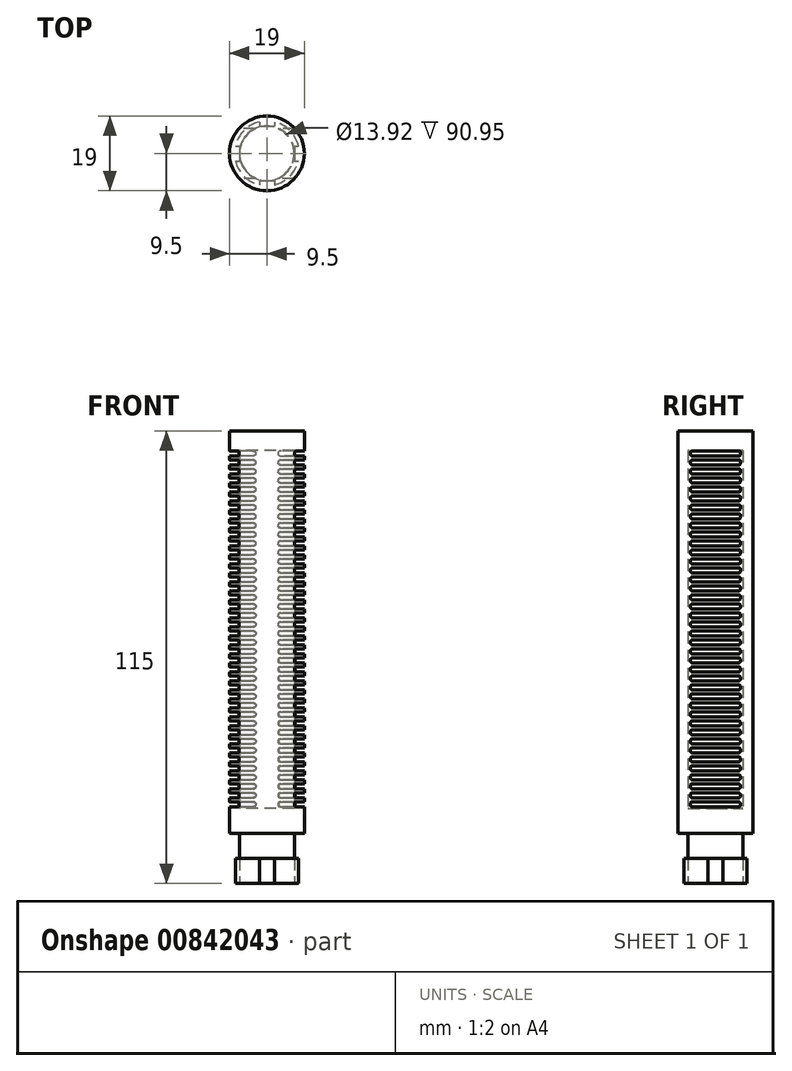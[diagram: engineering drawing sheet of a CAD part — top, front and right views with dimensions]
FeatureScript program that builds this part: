
annotation { "Feature Type Name" : "Feature", "Feature Type Description" : "" }
export const myFeature = defineFeature(function(context is Context, id is Id, definition is map)
    precondition{}
    {
        {
            var Q0;
            Q0=qCreatedBy(makeId("Top.planeOp"),FACE);
            var sketch = newSketch(context, id + "F0", { "sketchPlane" : qUnion([Q0])});
            skCircle(sketch, "E0", {"center": v(0, 0) * mm, "radius": 9.5 * mm});
            skSolve(sketch);
        }
        {
            var Q0;
            Q0=qSketchRegion(id+"F0",true);
            extrude(context, id + "F1", {"entities" : qUnion([Q0]), "depth" : 115 * mm, "offsetDistance" : 25.4 * mm});
        }
        {
            var Q0;
            Q0=qCreatedBy(makeId("Top.planeOp"),FACE);
            var sketch = newSketch(context, id + "F2", { "sketchPlane" : qUnion([Q0])});
            skCircle(sketch, "E1", {"center": v(0, 0) * mm, "radius": 9.5 * mm});
            skCircle(sketch, "E2.0", {"center": v(0, 0) * mm, "radius": 6.96 * mm});
            skSolve(sketch);
        }
        {
            var Q0;
            Q0=makeQuery(id+"F2.imprint","IMPRINT",FACE,{"disambiguationData":[TD([[makeQuery(id+"F2.imprint","IMPRINT",EDGE,{"derivedFrom":sQuery(id+"F2.wireOp",EDGE,"E1")}),1.0]])]});
            extrude(context, id + "F3", {"entities" : qUnion([Q0]), "depth" : 12.7 * mm, "offsetDistance" : 25.4 * mm, "hasSecondDirection" : true, "secondDirectionOppositeDirection" : true, "secondDirectionDepth" : -6.35 * mm});
        }
        {
            var Q0;
            Q0=makeQuery(id+"F3.opExtrude","SWEPT_BODY",BODY,{"disambiguationData":[OSD([sQuery(id+"F2.wireOp",EDGE,"E1"),sQuery(id+"F2.wireOp",EDGE,"E2.0")])]});
            var Q1;
            Q1=makeQuery(id+"F1.opExtrude","SWEPT_BODY",BODY,{"disambiguationData":[OSD([sQuery(id+"F0.wireOp",EDGE,"E0")])]});
            booleanBodies(context, id + "F4", {"operationType" : BooleanOperationType.SUBTRACTION, "tools" : qUnion([Q0]), "targets" : qUnion([Q1])});
        }
        {
            var Q0;
            Q0=qCreatedBy(makeId("Top.planeOp"),FACE);
            var sketch = newSketch(context, id + "F5", { "sketchPlane" : qUnion([Q0])});
            skCircle(sketch, "E3", {"center": v(0, 0) * mm, "radius": 9.5 * mm});
            skCircle(sketch, "E4.0", {"center": v(0, 0) * mm, "radius": 8.23 * mm});
            skSolve(sketch);
        }
        {
            var Q0;
            Q0=makeQuery(id+"F5.imprint","IMPRINT",FACE,{"disambiguationData":[TD([[makeQuery(id+"F5.imprint","IMPRINT",EDGE,{"derivedFrom":sQuery(id+"F5.wireOp",EDGE,"E3")}),1.0]])]});
            extrude(context, id + "F6", {"entities" : qUnion([Q0]), "depth" : 6.35 * mm, "offsetDistance" : 25.4 * mm});
        }
        {
            var Q0;
            Q0=makeQuery(id+"F6.opExtrude","SWEPT_BODY",BODY,{"disambiguationData":[OSD([sQuery(id+"F5.wireOp",EDGE,"E3"),sQuery(id+"F5.wireOp",EDGE,"E4.0")])]});
            var Q1;
            Q1=makeQuery(id+"F1.opExtrude","SWEPT_BODY",BODY,{"disambiguationData":[OSD([sQuery(id+"F0.wireOp",EDGE,"E0")])]});
            booleanBodies(context, id + "F7", {"operationType" : BooleanOperationType.SUBTRACTION, "tools" : qUnion([Q0]), "targets" : qUnion([Q1])});
        }
        {
            var Q0;
            Q0=qCreatedBy(makeId("Top.planeOp"),FACE);
            var sketch = newSketch(context, id + "F8", { "sketchPlane" : qUnion([Q0])});
            skCircle(sketch, "E5", {"center": v(0, 0) * mm, "radius": 9.5 * mm, "construction": true});
            skCircle(sketch, "E6.0", {"center": v(0, 0) * mm, "radius": 6.96 * mm, "construction": true});
            skLineSegment(sketch, "E7.bottom", {"start": v(-1.9, 10.77) * mm, "end": v(1.9, 10.77) * mm});
            skLineSegment(sketch, "E7.top", {"start": v(-1.9, 6.96) * mm, "end": v(1.9, 6.96) * mm});
            skLineSegment(sketch, "E7.left", {"start": v(-1.9, 10.77) * mm, "end": v(-1.9, 6.96) * mm});
            skLineSegment(sketch, "E7.right", {"start": v(1.9, 10.77) * mm, "end": v(1.9, 6.96) * mm});
            skPoint(sketch, "E8", {"position": v(0, 6.96) * mm});
            skLineSegment(sketch, "E9.bottom", {"start": v(-9.5, 9.5) * mm, "end": v(9.5, 9.5) * mm, "construction": true});
            skLineSegment(sketch, "E9.top", {"start": v(-9.5, -9.5) * mm, "end": v(9.5, -9.5) * mm, "construction": true});
            skLineSegment(sketch, "E9.left", {"start": v(-9.5, 9.5) * mm, "end": v(-9.5, -9.5) * mm, "construction": true});
            skLineSegment(sketch, "E9.right", {"start": v(9.5, 9.5) * mm, "end": v(9.5, -9.5) * mm, "construction": true});
            skPoint(sketch, "E10", {"position": v(0, -9.5) * mm});
            skPoint(sketch, "E11", {"position": v(9.5, 0) * mm});
            skLineSegment(sketch, "E12.0", {"start": v(-6.96, 6.96) * mm, "end": v(-6.96, -6.96) * mm, "construction": true});
            skLineSegment(sketch, "E12.1", {"start": v(-6.96, 6.96) * mm, "end": v(6.96, 6.96) * mm, "construction": true});
            skLineSegment(sketch, "E12.2", {"start": v(6.96, 6.96) * mm, "end": v(6.96, -6.96) * mm, "construction": true});
            skLineSegment(sketch, "E12.3", {"start": v(-6.96, -6.96) * mm, "end": v(6.96, -6.96) * mm, "construction": true});
            skLineSegment(sketch, "E13.bottom", {"start": v(6.96, 1.9) * mm, "end": v(10.77, 1.9) * mm});
            skLineSegment(sketch, "E13.top", {"start": v(6.96, -1.9) * mm, "end": v(10.77, -1.9) * mm});
            skLineSegment(sketch, "E13.left", {"start": v(6.96, 1.9) * mm, "end": v(6.96, -1.9) * mm});
            skLineSegment(sketch, "E13.right", {"start": v(10.77, 1.9) * mm, "end": v(10.77, -1.9) * mm});
            skPoint(sketch, "E14", {"position": v(6.96, 0) * mm});
            skLineSegment(sketch, "E15.bottom", {"start": v(-1.9, -6.96) * mm, "end": v(1.9, -6.96) * mm});
            skLineSegment(sketch, "E15.top", {"start": v(-1.9, -10.77) * mm, "end": v(1.9, -10.77) * mm});
            skLineSegment(sketch, "E15.left", {"start": v(-1.9, -6.96) * mm, "end": v(-1.9, -10.77) * mm});
            skLineSegment(sketch, "E15.right", {"start": v(1.9, -6.96) * mm, "end": v(1.9, -10.77) * mm});
            skPoint(sketch, "E16", {"position": v(0, -6.96) * mm});
            skLineSegment(sketch, "E17.bottom", {"start": v(-10.77, 1.9) * mm, "end": v(-6.96, 1.9) * mm});
            skLineSegment(sketch, "E17.top", {"start": v(-10.77, -1.9) * mm, "end": v(-6.96, -1.9) * mm});
            skLineSegment(sketch, "E17.left", {"start": v(-10.77, 1.9) * mm, "end": v(-10.77, -1.9) * mm});
            skLineSegment(sketch, "E17.right", {"start": v(-6.96, 1.9) * mm, "end": v(-6.96, -1.9) * mm});
            skPoint(sketch, "E18", {"position": v(-6.96, 0) * mm});
            skSolve(sketch);
        }
        {
            var Q0;
            Q0=makeQuery(id+"F8.imprint","IMPRINT",FACE,{"disambiguationData":[TD([[makeQuery(id+"F8.imprint","IMPRINT",EDGE,{"derivedFrom":sQuery(id+"F8.wireOp",EDGE,"E17.bottom")}),-1.0]])]});
            var Q1;
            Q1=makeQuery(id+"F8.imprint","IMPRINT",FACE,{"disambiguationData":[TD([[makeQuery(id+"F8.imprint","IMPRINT",EDGE,{"derivedFrom":sQuery(id+"F8.wireOp",EDGE,"E7.bottom")}),-1.0]])]});
            var Q2;
            Q2=makeQuery(id+"F8.imprint","IMPRINT",FACE,{"disambiguationData":[TD([[makeQuery(id+"F8.imprint","IMPRINT",EDGE,{"derivedFrom":sQuery(id+"F8.wireOp",EDGE,"E13.bottom")}),-1.0]])]});
            var Q3;
            Q3=makeQuery(id+"F8.imprint","IMPRINT",FACE,{"disambiguationData":[TD([[makeQuery(id+"F8.imprint","IMPRINT",EDGE,{"derivedFrom":sQuery(id+"F8.wireOp",EDGE,"E15.bottom")}),-1.0]])]});
            extrude(context, id + "F9", {"entities" : qUnion([Q0, Q1, Q2, Q3]), "depth" : 6.35 * mm, "offsetDistance" : 25.4 * mm});
        }
        {
            var Q0;
            Q0=makeQuery(id+"F9.opExtrude","SWEPT_BODY",BODY,{"disambiguationData":[OSD([sQuery(id+"F8.wireOp",EDGE,"E7.bottom"),sQuery(id+"F8.wireOp",EDGE,"E7.top"),sQuery(id+"F8.wireOp",EDGE,"E7.left"),sQuery(id+"F8.wireOp",EDGE,"E7.right")])]});
            var Q1;
            Q1=makeQuery(id+"F9.opExtrude","SWEPT_BODY",BODY,{"disambiguationData":[OSD([sQuery(id+"F8.wireOp",EDGE,"E13.bottom"),sQuery(id+"F8.wireOp",EDGE,"E13.top"),sQuery(id+"F8.wireOp",EDGE,"E13.left"),sQuery(id+"F8.wireOp",EDGE,"E13.right")])]});
            var Q2;
            Q2=makeQuery(id+"F9.opExtrude","SWEPT_BODY",BODY,{"disambiguationData":[OSD([sQuery(id+"F8.wireOp",EDGE,"E15.bottom"),sQuery(id+"F8.wireOp",EDGE,"E15.top"),sQuery(id+"F8.wireOp",EDGE,"E15.left"),sQuery(id+"F8.wireOp",EDGE,"E15.right")])]});
            var Q3;
            Q3=makeQuery(id+"F9.opExtrude","SWEPT_BODY",BODY,{"disambiguationData":[OSD([sQuery(id+"F8.wireOp",EDGE,"E17.bottom"),sQuery(id+"F8.wireOp",EDGE,"E17.top"),sQuery(id+"F8.wireOp",EDGE,"E17.left"),sQuery(id+"F8.wireOp",EDGE,"E17.right")])]});
            var Q4;
            Q4=makeQuery(id+"F1.opExtrude","SWEPT_BODY",BODY,{"disambiguationData":[OSD([sQuery(id+"F0.wireOp",EDGE,"E0")])]});
            booleanBodies(context, id + "F10", {"operationType" : BooleanOperationType.SUBTRACTION, "tools" : qUnion([Q0, Q1, Q2, Q3]), "targets" : qUnion([Q4])});
        }
        {
            var Q0;
            Q0=qCreatedBy(makeId("Top.planeOp"),FACE);
            var sketch = newSketch(context, id + "F11", { "sketchPlane" : qUnion([Q0])});
            skCircle(sketch, "E19", {"center": v(0, 0) * mm, "radius": 9.5 * mm, "construction": true});
            skCircle(sketch, "E20.0", {"center": v(0, 0) * mm, "radius": 6.96 * mm});
            skSolve(sketch);
        }
        {
            var Q0;
            Q0=makeQuery(id+"F11.imprint","IMPRINT",FACE,{"disambiguationData":[TD([[makeQuery(id+"F11.imprint","IMPRINT",EDGE,{"derivedFrom":sQuery(id+"F11.wireOp",EDGE,"E20.0")}),1.0]])]});
            extrude(context, id + "F12", {"entities" : qUnion([Q0]), "operationType" : NewBodyOperationType.REMOVE, "depth" : 110 * mm, "offsetDistance" : 25.4 * mm, "hasSecondDirection" : true, "secondDirectionOppositeDirection" : true, "secondDirectionDepth" : -19.05 * mm});
        }
        {
            var Q0;
            Q0=qCreatedBy(makeId("Right.planeOp"),FACE);
            var sketch = newSketch(context, id + "F13", { "sketchPlane" : qUnion([Q0])});
            skLineSegment(sketch, "E21.bottom", {"start": v(5.91, 109.9) * mm, "end": v(-5.91, 109.9) * mm});
            skLineSegment(sketch, "E21.top", {"start": v(5.91, 108.63) * mm, "end": v(-5.91, 108.63) * mm});
            skLineSegment(sketch, "E21.left", {"start": v(6.35, 109.46) * mm, "end": v(6.35, 109.06) * mm});
            skLineSegment(sketch, "E21.right", {"start": v(-6.35, 109.46) * mm, "end": v(-6.35, 109.06) * mm});
            skPoint(sketch, "E22", {"position": v(0, 109.9) * mm});
            skPoint(sketch, "E23.visualSharp", {"position": v(6.35, 109.9) * mm});
            skArc(sketch, "E23.filletArc", {"start": v(6.35, 109.46) * mm, "mid": v(6.22, 109.77) * mm, "end": v(5.91, 109.9) * mm});
            skPoint(sketch, "E24.visualSharp", {"position": v(6.35, 108.63) * mm});
            skArc(sketch, "E24.filletArc", {"start": v(5.91, 108.63) * mm, "mid": v(6.22, 108.75) * mm, "end": v(6.35, 109.06) * mm});
            skPoint(sketch, "E25.visualSharp", {"position": v(-6.35, 108.63) * mm});
            skArc(sketch, "E25.filletArc", {"start": v(-6.35, 109.06) * mm, "mid": v(-6.22, 108.75) * mm, "end": v(-5.91, 108.63) * mm});
            skPoint(sketch, "E26.visualSharp", {"position": v(-6.35, 109.9) * mm});
            skArc(sketch, "E26.filletArc", {"start": v(-5.91, 109.9) * mm, "mid": v(-6.22, 109.77) * mm, "end": v(-6.35, 109.46) * mm});
            skArc(sketch, "E27.1.0.0", {"start": v(6.35, 107.17) * mm, "mid": v(6.22, 107.48) * mm, "end": v(5.9, 107.6) * mm});
            skLineSegment(sketch, "E27.1.0.1", {"start": v(5.9, 107.6) * mm, "end": v(-5.91, 107.6) * mm});
            skArc(sketch, "E27.1.0.2", {"start": v(-5.91, 107.6) * mm, "mid": v(-6.22, 107.48) * mm, "end": v(-6.35, 107.17) * mm});
            skLineSegment(sketch, "E27.1.0.3", {"start": v(-6.35, 107.17) * mm, "end": v(-6.35, 106.78) * mm});
            skArc(sketch, "E27.1.0.4", {"start": v(-6.35, 106.78) * mm, "mid": v(-6.22, 106.47) * mm, "end": v(-5.91, 106.34) * mm});
            skLineSegment(sketch, "E27.1.0.5", {"start": v(5.9, 106.34) * mm, "end": v(-5.91, 106.34) * mm});
            skArc(sketch, "E27.1.0.6", {"start": v(5.9, 106.34) * mm, "mid": v(6.22, 106.47) * mm, "end": v(6.35, 106.78) * mm});
            skLineSegment(sketch, "E27.1.0.7", {"start": v(6.35, 107.17) * mm, "end": v(6.35, 106.78) * mm});
            skArc(sketch, "E27.2.0.0", {"start": v(6.35, 104.88) * mm, "mid": v(6.22, 105.2) * mm, "end": v(5.9, 105.32) * mm});
            skLineSegment(sketch, "E27.2.0.1", {"start": v(5.9, 105.32) * mm, "end": v(-5.91, 105.32) * mm});
            skArc(sketch, "E27.2.0.2", {"start": v(-5.91, 105.32) * mm, "mid": v(-6.22, 105.2) * mm, "end": v(-6.35, 104.88) * mm});
            skLineSegment(sketch, "E27.2.0.3", {"start": v(-6.35, 104.88) * mm, "end": v(-6.35, 104.5) * mm});
            skArc(sketch, "E27.2.0.4", {"start": v(-6.35, 104.5) * mm, "mid": v(-6.22, 104.18) * mm, "end": v(-5.91, 104.05) * mm});
            skLineSegment(sketch, "E27.2.0.5", {"start": v(5.9, 104.05) * mm, "end": v(-5.91, 104.05) * mm});
            skArc(sketch, "E27.2.0.6", {"start": v(5.9, 104.05) * mm, "mid": v(6.22, 104.18) * mm, "end": v(6.35, 104.5) * mm});
            skLineSegment(sketch, "E27.2.0.7", {"start": v(6.35, 104.88) * mm, "end": v(6.35, 104.5) * mm});
            skArc(sketch, "E27.3.0.0", {"start": v(6.35, 102.6) * mm, "mid": v(6.22, 102.9) * mm, "end": v(5.9, 103.04) * mm});
            skLineSegment(sketch, "E27.3.0.1", {"start": v(5.9, 103.04) * mm, "end": v(-5.91, 103.04) * mm});
            skArc(sketch, "E27.3.0.2", {"start": v(-5.91, 103.04) * mm, "mid": v(-6.22, 102.9) * mm, "end": v(-6.35, 102.6) * mm});
            skLineSegment(sketch, "E27.3.0.3", {"start": v(-6.35, 102.6) * mm, "end": v(-6.35, 102.2) * mm});
            skArc(sketch, "E27.3.0.4", {"start": v(-6.35, 102.2) * mm, "mid": v(-6.22, 101.9) * mm, "end": v(-5.91, 101.77) * mm});
            skLineSegment(sketch, "E27.3.0.5", {"start": v(5.9, 101.77) * mm, "end": v(-5.91, 101.77) * mm});
            skArc(sketch, "E27.3.0.6", {"start": v(5.9, 101.77) * mm, "mid": v(6.22, 101.9) * mm, "end": v(6.35, 102.2) * mm});
            skLineSegment(sketch, "E27.3.0.7", {"start": v(6.35, 102.6) * mm, "end": v(6.35, 102.2) * mm});
            skArc(sketch, "E27.4.0.0", {"start": v(6.35, 100.31) * mm, "mid": v(6.22, 100.62) * mm, "end": v(5.9, 100.75) * mm});
            skLineSegment(sketch, "E27.4.0.1", {"start": v(5.9, 100.75) * mm, "end": v(-5.91, 100.75) * mm});
            skArc(sketch, "E27.4.0.2", {"start": v(-5.91, 100.75) * mm, "mid": v(-6.22, 100.62) * mm, "end": v(-6.35, 100.31) * mm});
            skLineSegment(sketch, "E27.4.0.3", {"start": v(-6.35, 100.31) * mm, "end": v(-6.35, 99.92) * mm});
            skArc(sketch, "E27.4.0.4", {"start": v(-6.35, 99.92) * mm, "mid": v(-6.22, 99.61) * mm, "end": v(-5.91, 99.48) * mm});
            skLineSegment(sketch, "E27.4.0.5", {"start": v(5.9, 99.48) * mm, "end": v(-5.91, 99.48) * mm});
            skArc(sketch, "E27.4.0.6", {"start": v(5.9, 99.48) * mm, "mid": v(6.22, 99.61) * mm, "end": v(6.35, 99.92) * mm});
            skLineSegment(sketch, "E27.4.0.7", {"start": v(6.35, 100.31) * mm, "end": v(6.35, 99.92) * mm});
            skArc(sketch, "E27.5.0.0", {"start": v(6.35, 98.03) * mm, "mid": v(6.22, 98.34) * mm, "end": v(5.9, 98.47) * mm});
            skLineSegment(sketch, "E27.5.0.1", {"start": v(5.9, 98.47) * mm, "end": v(-5.91, 98.47) * mm});
            skArc(sketch, "E27.5.0.2", {"start": v(-5.91, 98.47) * mm, "mid": v(-6.23, 98.34) * mm, "end": v(-6.35, 98.03) * mm});
            skLineSegment(sketch, "E27.5.0.3", {"start": v(-6.35, 98.03) * mm, "end": v(-6.35, 97.63) * mm});
            skArc(sketch, "E27.5.0.4", {"start": v(-6.35, 97.63) * mm, "mid": v(-6.23, 97.32) * mm, "end": v(-5.91, 97.2) * mm});
            skLineSegment(sketch, "E27.5.0.5", {"start": v(5.9, 97.2) * mm, "end": v(-5.91, 97.2) * mm});
            skArc(sketch, "E27.5.0.6", {"start": v(5.9, 97.2) * mm, "mid": v(6.22, 97.32) * mm, "end": v(6.35, 97.63) * mm});
            skLineSegment(sketch, "E27.5.0.7", {"start": v(6.35, 98.03) * mm, "end": v(6.35, 97.63) * mm});
            skArc(sketch, "E27.6.0.0", {"start": v(6.34, 95.74) * mm, "mid": v(6.22, 96.05) * mm, "end": v(5.9, 96.18) * mm});
            skLineSegment(sketch, "E27.6.0.1", {"start": v(5.9, 96.18) * mm, "end": v(-5.92, 96.18) * mm});
            skArc(sketch, "E27.6.0.2", {"start": v(-5.92, 96.18) * mm, "mid": v(-6.23, 96.05) * mm, "end": v(-6.36, 95.74) * mm});
            skLineSegment(sketch, "E27.6.0.3", {"start": v(-6.36, 95.74) * mm, "end": v(-6.36, 95.35) * mm});
            skArc(sketch, "E27.6.0.4", {"start": v(-6.36, 95.35) * mm, "mid": v(-6.23, 95.04) * mm, "end": v(-5.92, 94.9) * mm});
            skLineSegment(sketch, "E27.6.0.5", {"start": v(5.9, 94.9) * mm, "end": v(-5.92, 94.9) * mm});
            skArc(sketch, "E27.6.0.6", {"start": v(5.9, 94.9) * mm, "mid": v(6.22, 95.04) * mm, "end": v(6.34, 95.35) * mm});
            skLineSegment(sketch, "E27.6.0.7", {"start": v(6.34, 95.74) * mm, "end": v(6.34, 95.35) * mm});
            skArc(sketch, "E27.7.0.0", {"start": v(6.34, 93.45) * mm, "mid": v(6.22, 93.77) * mm, "end": v(5.9, 93.9) * mm});
            skLineSegment(sketch, "E27.7.0.1", {"start": v(5.9, 93.9) * mm, "end": v(-5.92, 93.9) * mm});
            skArc(sketch, "E27.7.0.2", {"start": v(-5.92, 93.9) * mm, "mid": v(-6.23, 93.77) * mm, "end": v(-6.36, 93.45) * mm});
            skLineSegment(sketch, "E27.7.0.3", {"start": v(-6.36, 93.45) * mm, "end": v(-6.36, 93.06) * mm});
            skArc(sketch, "E27.7.0.4", {"start": v(-6.36, 93.06) * mm, "mid": v(-6.23, 92.75) * mm, "end": v(-5.92, 92.62) * mm});
            skLineSegment(sketch, "E27.7.0.5", {"start": v(5.9, 92.62) * mm, "end": v(-5.92, 92.62) * mm});
            skArc(sketch, "E27.7.0.6", {"start": v(5.9, 92.62) * mm, "mid": v(6.22, 92.75) * mm, "end": v(6.34, 93.06) * mm});
            skLineSegment(sketch, "E27.7.0.7", {"start": v(6.34, 93.45) * mm, "end": v(6.34, 93.06) * mm});
            skArc(sketch, "E27.8.0.0", {"start": v(6.34, 91.17) * mm, "mid": v(6.21, 91.48) * mm, "end": v(5.9, 91.6) * mm});
            skLineSegment(sketch, "E27.8.0.1", {"start": v(5.9, 91.6) * mm, "end": v(-5.92, 91.6) * mm});
            skArc(sketch, "E27.8.0.2", {"start": v(-5.92, 91.6) * mm, "mid": v(-6.23, 91.48) * mm, "end": v(-6.36, 91.17) * mm});
            skLineSegment(sketch, "E27.8.0.3", {"start": v(-6.36, 91.17) * mm, "end": v(-6.36, 90.78) * mm});
            skArc(sketch, "E27.8.0.4", {"start": v(-6.36, 90.78) * mm, "mid": v(-6.23, 90.47) * mm, "end": v(-5.92, 90.34) * mm});
            skLineSegment(sketch, "E27.8.0.5", {"start": v(5.9, 90.34) * mm, "end": v(-5.92, 90.34) * mm});
            skArc(sketch, "E27.8.0.6", {"start": v(5.9, 90.34) * mm, "mid": v(6.21, 90.47) * mm, "end": v(6.34, 90.78) * mm});
            skLineSegment(sketch, "E27.8.0.7", {"start": v(6.34, 91.17) * mm, "end": v(6.34, 90.78) * mm});
            skArc(sketch, "E27.9.0.0", {"start": v(6.34, 88.88) * mm, "mid": v(6.21, 89.2) * mm, "end": v(5.9, 89.32) * mm});
            skLineSegment(sketch, "E27.9.0.1", {"start": v(5.9, 89.32) * mm, "end": v(-5.92, 89.32) * mm});
            skArc(sketch, "E27.9.0.2", {"start": v(-5.92, 89.32) * mm, "mid": v(-6.23, 89.2) * mm, "end": v(-6.36, 88.88) * mm});
            skLineSegment(sketch, "E27.9.0.3", {"start": v(-6.36, 88.88) * mm, "end": v(-6.36, 88.5) * mm});
            skArc(sketch, "E27.9.0.4", {"start": v(-6.36, 88.5) * mm, "mid": v(-6.23, 88.18) * mm, "end": v(-5.92, 88.05) * mm});
            skLineSegment(sketch, "E27.9.0.5", {"start": v(5.9, 88.05) * mm, "end": v(-5.92, 88.05) * mm});
            skArc(sketch, "E27.9.0.6", {"start": v(5.9, 88.05) * mm, "mid": v(6.21, 88.18) * mm, "end": v(6.34, 88.5) * mm});
            skLineSegment(sketch, "E27.9.0.7", {"start": v(6.34, 88.88) * mm, "end": v(6.34, 88.5) * mm});
            skArc(sketch, "E27.10.0.0", {"start": v(6.34, 86.6) * mm, "mid": v(6.21, 86.9) * mm, "end": v(5.9, 87.04) * mm});
            skLineSegment(sketch, "E27.10.0.1", {"start": v(5.9, 87.04) * mm, "end": v(-5.92, 87.04) * mm});
            skArc(sketch, "E27.10.0.2", {"start": v(-5.92, 87.04) * mm, "mid": v(-6.23, 86.9) * mm, "end": v(-6.36, 86.6) * mm});
            skLineSegment(sketch, "E27.10.0.3", {"start": v(-6.36, 86.6) * mm, "end": v(-6.36, 86.2) * mm});
            skArc(sketch, "E27.10.0.4", {"start": v(-6.36, 86.2) * mm, "mid": v(-6.23, 85.9) * mm, "end": v(-5.92, 85.77) * mm});
            skLineSegment(sketch, "E27.10.0.5", {"start": v(5.9, 85.77) * mm, "end": v(-5.92, 85.77) * mm});
            skArc(sketch, "E27.10.0.6", {"start": v(5.9, 85.77) * mm, "mid": v(6.21, 85.9) * mm, "end": v(6.34, 86.2) * mm});
            skLineSegment(sketch, "E27.10.0.7", {"start": v(6.34, 86.6) * mm, "end": v(6.34, 86.2) * mm});
            skArc(sketch, "E27.11.0.0", {"start": v(6.34, 84.31) * mm, "mid": v(6.21, 84.62) * mm, "end": v(5.9, 84.75) * mm});
            skLineSegment(sketch, "E27.11.0.1", {"start": v(5.9, 84.75) * mm, "end": v(-5.92, 84.75) * mm});
            skArc(sketch, "E27.11.0.2", {"start": v(-5.92, 84.75) * mm, "mid": v(-6.23, 84.62) * mm, "end": v(-6.36, 84.31) * mm});
            skLineSegment(sketch, "E27.11.0.3", {"start": v(-6.36, 84.31) * mm, "end": v(-6.36, 83.92) * mm});
            skArc(sketch, "E27.11.0.4", {"start": v(-6.36, 83.92) * mm, "mid": v(-6.23, 83.6) * mm, "end": v(-5.92, 83.48) * mm});
            skLineSegment(sketch, "E27.11.0.5", {"start": v(5.9, 83.48) * mm, "end": v(-5.92, 83.48) * mm});
            skArc(sketch, "E27.11.0.6", {"start": v(5.9, 83.48) * mm, "mid": v(6.21, 83.6) * mm, "end": v(6.34, 83.92) * mm});
            skLineSegment(sketch, "E27.11.0.7", {"start": v(6.34, 84.31) * mm, "end": v(6.34, 83.92) * mm});
            skArc(sketch, "E27.12.0.0", {"start": v(6.34, 82.02) * mm, "mid": v(6.21, 82.34) * mm, "end": v(5.9, 82.46) * mm});
            skLineSegment(sketch, "E27.12.0.1", {"start": v(5.9, 82.46) * mm, "end": v(-5.92, 82.46) * mm});
            skArc(sketch, "E27.12.0.2", {"start": v(-5.92, 82.46) * mm, "mid": v(-6.23, 82.34) * mm, "end": v(-6.36, 82.02) * mm});
            skLineSegment(sketch, "E27.12.0.3", {"start": v(-6.36, 82.02) * mm, "end": v(-6.36, 81.63) * mm});
            skArc(sketch, "E27.12.0.4", {"start": v(-6.36, 81.63) * mm, "mid": v(-6.23, 81.32) * mm, "end": v(-5.92, 81.2) * mm});
            skLineSegment(sketch, "E27.12.0.5", {"start": v(5.9, 81.2) * mm, "end": v(-5.92, 81.2) * mm});
            skArc(sketch, "E27.12.0.6", {"start": v(5.9, 81.2) * mm, "mid": v(6.21, 81.32) * mm, "end": v(6.34, 81.63) * mm});
            skLineSegment(sketch, "E27.12.0.7", {"start": v(6.34, 82.02) * mm, "end": v(6.34, 81.63) * mm});
            skArc(sketch, "E27.13.0.0", {"start": v(6.34, 79.74) * mm, "mid": v(6.21, 80.05) * mm, "end": v(5.9, 80.18) * mm});
            skLineSegment(sketch, "E27.13.0.1", {"start": v(5.9, 80.18) * mm, "end": v(-5.92, 80.18) * mm});
            skArc(sketch, "E27.13.0.2", {"start": v(-5.92, 80.18) * mm, "mid": v(-6.23, 80.05) * mm, "end": v(-6.36, 79.74) * mm});
            skLineSegment(sketch, "E27.13.0.3", {"start": v(-6.36, 79.74) * mm, "end": v(-6.36, 79.35) * mm});
            skArc(sketch, "E27.13.0.4", {"start": v(-6.36, 79.35) * mm, "mid": v(-6.23, 79.04) * mm, "end": v(-5.92, 78.9) * mm});
            skLineSegment(sketch, "E27.13.0.5", {"start": v(5.9, 78.9) * mm, "end": v(-5.92, 78.9) * mm});
            skArc(sketch, "E27.13.0.6", {"start": v(5.9, 78.9) * mm, "mid": v(6.21, 79.04) * mm, "end": v(6.34, 79.35) * mm});
            skLineSegment(sketch, "E27.13.0.7", {"start": v(6.34, 79.74) * mm, "end": v(6.34, 79.35) * mm});
            skArc(sketch, "E27.14.0.0", {"start": v(6.34, 77.45) * mm, "mid": v(6.2, 77.76) * mm, "end": v(5.9, 77.9) * mm});
            skLineSegment(sketch, "E27.14.0.1", {"start": v(5.9, 77.9) * mm, "end": v(-5.92, 77.9) * mm});
            skArc(sketch, "E27.14.0.2", {"start": v(-5.92, 77.9) * mm, "mid": v(-6.23, 77.76) * mm, "end": v(-6.36, 77.45) * mm});
            skLineSegment(sketch, "E27.14.0.3", {"start": v(-6.36, 77.45) * mm, "end": v(-6.36, 77.06) * mm});
            skArc(sketch, "E27.14.0.4", {"start": v(-6.36, 77.06) * mm, "mid": v(-6.23, 76.75) * mm, "end": v(-5.92, 76.62) * mm});
            skLineSegment(sketch, "E27.14.0.5", {"start": v(5.9, 76.62) * mm, "end": v(-5.92, 76.62) * mm});
            skArc(sketch, "E27.14.0.6", {"start": v(5.9, 76.62) * mm, "mid": v(6.2, 76.75) * mm, "end": v(6.34, 77.06) * mm});
            skLineSegment(sketch, "E27.14.0.7", {"start": v(6.34, 77.45) * mm, "end": v(6.34, 77.06) * mm});
            skArc(sketch, "E27.15.0.0", {"start": v(6.34, 75.17) * mm, "mid": v(6.2, 75.48) * mm, "end": v(5.9, 75.6) * mm});
            skLineSegment(sketch, "E27.15.0.1", {"start": v(5.9, 75.6) * mm, "end": v(-5.92, 75.6) * mm});
            skArc(sketch, "E27.15.0.2", {"start": v(-5.92, 75.6) * mm, "mid": v(-6.23, 75.48) * mm, "end": v(-6.36, 75.17) * mm});
            skLineSegment(sketch, "E27.15.0.3", {"start": v(-6.36, 75.17) * mm, "end": v(-6.36, 74.77) * mm});
            skArc(sketch, "E27.15.0.4", {"start": v(-6.36, 74.77) * mm, "mid": v(-6.23, 74.46) * mm, "end": v(-5.92, 74.34) * mm});
            skLineSegment(sketch, "E27.15.0.5", {"start": v(5.9, 74.34) * mm, "end": v(-5.92, 74.34) * mm});
            skArc(sketch, "E27.15.0.6", {"start": v(5.9, 74.34) * mm, "mid": v(6.2, 74.46) * mm, "end": v(6.34, 74.77) * mm});
            skLineSegment(sketch, "E27.15.0.7", {"start": v(6.34, 75.17) * mm, "end": v(6.34, 74.77) * mm});
            skArc(sketch, "E27.16.0.0", {"start": v(6.34, 72.88) * mm, "mid": v(6.2, 73.2) * mm, "end": v(5.9, 73.32) * mm});
            skLineSegment(sketch, "E27.16.0.1", {"start": v(5.9, 73.32) * mm, "end": v(-5.92, 73.32) * mm});
            skArc(sketch, "E27.16.0.2", {"start": v(-5.92, 73.32) * mm, "mid": v(-6.23, 73.2) * mm, "end": v(-6.36, 72.88) * mm});
            skLineSegment(sketch, "E27.16.0.3", {"start": v(-6.36, 72.88) * mm, "end": v(-6.36, 72.49) * mm});
            skArc(sketch, "E27.16.0.4", {"start": v(-6.36, 72.49) * mm, "mid": v(-6.23, 72.18) * mm, "end": v(-5.92, 72.05) * mm});
            skLineSegment(sketch, "E27.16.0.5", {"start": v(5.9, 72.05) * mm, "end": v(-5.92, 72.05) * mm});
            skArc(sketch, "E27.16.0.6", {"start": v(5.9, 72.05) * mm, "mid": v(6.2, 72.18) * mm, "end": v(6.34, 72.49) * mm});
            skLineSegment(sketch, "E27.16.0.7", {"start": v(6.34, 72.88) * mm, "end": v(6.34, 72.49) * mm});
            skArc(sketch, "E27.17.0.0", {"start": v(6.34, 70.6) * mm, "mid": v(6.2, 70.9) * mm, "end": v(5.9, 71.03) * mm});
            skLineSegment(sketch, "E27.17.0.1", {"start": v(5.9, 71.03) * mm, "end": v(-5.93, 71.03) * mm});
            skArc(sketch, "E27.17.0.2", {"start": v(-5.93, 71.03) * mm, "mid": v(-6.24, 70.9) * mm, "end": v(-6.36, 70.6) * mm});
            skLineSegment(sketch, "E27.17.0.3", {"start": v(-6.36, 70.6) * mm, "end": v(-6.36, 70.2) * mm});
            skArc(sketch, "E27.17.0.4", {"start": v(-6.36, 70.2) * mm, "mid": v(-6.24, 69.9) * mm, "end": v(-5.93, 69.76) * mm});
            skLineSegment(sketch, "E27.17.0.5", {"start": v(5.9, 69.76) * mm, "end": v(-5.93, 69.76) * mm});
            skArc(sketch, "E27.17.0.6", {"start": v(5.9, 69.76) * mm, "mid": v(6.2, 69.9) * mm, "end": v(6.34, 70.2) * mm});
            skLineSegment(sketch, "E27.17.0.7", {"start": v(6.34, 70.6) * mm, "end": v(6.34, 70.2) * mm});
            skArc(sketch, "E27.18.0.0", {"start": v(6.33, 68.3) * mm, "mid": v(6.2, 68.62) * mm, "end": v(5.9, 68.75) * mm});
            skLineSegment(sketch, "E27.18.0.1", {"start": v(5.9, 68.75) * mm, "end": v(-5.93, 68.75) * mm});
            skArc(sketch, "E27.18.0.2", {"start": v(-5.93, 68.75) * mm, "mid": v(-6.24, 68.62) * mm, "end": v(-6.37, 68.3) * mm});
            skLineSegment(sketch, "E27.18.0.3", {"start": v(-6.37, 68.3) * mm, "end": v(-6.37, 67.92) * mm});
            skArc(sketch, "E27.18.0.4", {"start": v(-6.37, 67.92) * mm, "mid": v(-6.24, 67.6) * mm, "end": v(-5.93, 67.48) * mm});
            skLineSegment(sketch, "E27.18.0.5", {"start": v(5.9, 67.48) * mm, "end": v(-5.93, 67.48) * mm});
            skArc(sketch, "E27.18.0.6", {"start": v(5.9, 67.48) * mm, "mid": v(6.2, 67.6) * mm, "end": v(6.33, 67.92) * mm});
            skLineSegment(sketch, "E27.18.0.7", {"start": v(6.33, 68.3) * mm, "end": v(6.33, 67.92) * mm});
            skArc(sketch, "E27.19.0.0", {"start": v(6.33, 66.02) * mm, "mid": v(6.2, 66.33) * mm, "end": v(5.9, 66.46) * mm});
            skLineSegment(sketch, "E27.19.0.1", {"start": v(5.9, 66.46) * mm, "end": v(-5.93, 66.46) * mm});
            skArc(sketch, "E27.19.0.2", {"start": v(-5.93, 66.46) * mm, "mid": v(-6.24, 66.33) * mm, "end": v(-6.37, 66.02) * mm});
            skLineSegment(sketch, "E27.19.0.3", {"start": v(-6.37, 66.02) * mm, "end": v(-6.37, 65.63) * mm});
            skArc(sketch, "E27.19.0.4", {"start": v(-6.37, 65.63) * mm, "mid": v(-6.24, 65.32) * mm, "end": v(-5.93, 65.2) * mm});
            skLineSegment(sketch, "E27.19.0.5", {"start": v(5.9, 65.2) * mm, "end": v(-5.93, 65.2) * mm});
            skArc(sketch, "E27.19.0.6", {"start": v(5.9, 65.2) * mm, "mid": v(6.2, 65.32) * mm, "end": v(6.33, 65.63) * mm});
            skLineSegment(sketch, "E27.19.0.7", {"start": v(6.33, 66.02) * mm, "end": v(6.33, 65.63) * mm});
            skArc(sketch, "E27.20.0.0", {"start": v(6.33, 63.74) * mm, "mid": v(6.2, 64.05) * mm, "end": v(5.9, 64.18) * mm});
            skLineSegment(sketch, "E27.20.0.1", {"start": v(5.9, 64.18) * mm, "end": v(-5.93, 64.18) * mm});
            skArc(sketch, "E27.20.0.2", {"start": v(-5.93, 64.18) * mm, "mid": v(-6.24, 64.05) * mm, "end": v(-6.37, 63.74) * mm});
            skLineSegment(sketch, "E27.20.0.3", {"start": v(-6.37, 63.74) * mm, "end": v(-6.37, 63.34) * mm});
            skArc(sketch, "E27.20.0.4", {"start": v(-6.37, 63.34) * mm, "mid": v(-6.24, 63.03) * mm, "end": v(-5.93, 62.9) * mm});
            skLineSegment(sketch, "E27.20.0.5", {"start": v(5.9, 62.9) * mm, "end": v(-5.93, 62.9) * mm});
            skArc(sketch, "E27.20.0.6", {"start": v(5.9, 62.9) * mm, "mid": v(6.2, 63.03) * mm, "end": v(6.33, 63.34) * mm});
            skLineSegment(sketch, "E27.20.0.7", {"start": v(6.33, 63.74) * mm, "end": v(6.33, 63.34) * mm});
            skArc(sketch, "E27.21.0.0", {"start": v(6.33, 61.45) * mm, "mid": v(6.2, 61.76) * mm, "end": v(5.9, 61.89) * mm});
            skLineSegment(sketch, "E27.21.0.1", {"start": v(5.9, 61.89) * mm, "end": v(-5.93, 61.89) * mm});
            skArc(sketch, "E27.21.0.2", {"start": v(-5.93, 61.89) * mm, "mid": v(-6.24, 61.76) * mm, "end": v(-6.37, 61.45) * mm});
            skLineSegment(sketch, "E27.21.0.3", {"start": v(-6.37, 61.45) * mm, "end": v(-6.37, 61.06) * mm});
            skArc(sketch, "E27.21.0.4", {"start": v(-6.37, 61.06) * mm, "mid": v(-6.24, 60.75) * mm, "end": v(-5.93, 60.62) * mm});
            skLineSegment(sketch, "E27.21.0.5", {"start": v(5.9, 60.62) * mm, "end": v(-5.93, 60.62) * mm});
            skArc(sketch, "E27.21.0.6", {"start": v(5.9, 60.62) * mm, "mid": v(6.2, 60.75) * mm, "end": v(6.33, 61.06) * mm});
            skLineSegment(sketch, "E27.21.0.7", {"start": v(6.33, 61.45) * mm, "end": v(6.33, 61.06) * mm});
            skArc(sketch, "E27.22.0.0", {"start": v(6.33, 59.16) * mm, "mid": v(6.2, 59.48) * mm, "end": v(5.9, 59.6) * mm});
            skLineSegment(sketch, "E27.22.0.1", {"start": v(5.9, 59.6) * mm, "end": v(-5.93, 59.6) * mm});
            skArc(sketch, "E27.22.0.2", {"start": v(-5.93, 59.6) * mm, "mid": v(-6.24, 59.48) * mm, "end": v(-6.37, 59.16) * mm});
            skLineSegment(sketch, "E27.22.0.3", {"start": v(-6.37, 59.16) * mm, "end": v(-6.37, 58.77) * mm});
            skArc(sketch, "E27.22.0.4", {"start": v(-6.37, 58.77) * mm, "mid": v(-6.24, 58.46) * mm, "end": v(-5.93, 58.33) * mm});
            skLineSegment(sketch, "E27.22.0.5", {"start": v(5.9, 58.33) * mm, "end": v(-5.93, 58.33) * mm});
            skArc(sketch, "E27.22.0.6", {"start": v(5.9, 58.33) * mm, "mid": v(6.2, 58.46) * mm, "end": v(6.33, 58.77) * mm});
            skLineSegment(sketch, "E27.22.0.7", {"start": v(6.33, 59.16) * mm, "end": v(6.33, 58.77) * mm});
            skArc(sketch, "E27.23.0.0", {"start": v(6.33, 56.88) * mm, "mid": v(6.2, 57.19) * mm, "end": v(5.9, 57.32) * mm});
            skLineSegment(sketch, "E27.23.0.1", {"start": v(5.9, 57.32) * mm, "end": v(-5.93, 57.32) * mm});
            skArc(sketch, "E27.23.0.2", {"start": v(-5.93, 57.32) * mm, "mid": v(-6.24, 57.19) * mm, "end": v(-6.37, 56.88) * mm});
            skLineSegment(sketch, "E27.23.0.3", {"start": v(-6.37, 56.88) * mm, "end": v(-6.37, 56.49) * mm});
            skArc(sketch, "E27.23.0.4", {"start": v(-6.37, 56.49) * mm, "mid": v(-6.24, 56.18) * mm, "end": v(-5.93, 56.05) * mm});
            skLineSegment(sketch, "E27.23.0.5", {"start": v(5.9, 56.05) * mm, "end": v(-5.93, 56.05) * mm});
            skArc(sketch, "E27.23.0.6", {"start": v(5.9, 56.05) * mm, "mid": v(6.2, 56.18) * mm, "end": v(6.33, 56.49) * mm});
            skLineSegment(sketch, "E27.23.0.7", {"start": v(6.33, 56.88) * mm, "end": v(6.33, 56.49) * mm});
            skArc(sketch, "E27.24.0.0", {"start": v(6.33, 54.6) * mm, "mid": v(6.2, 54.9) * mm, "end": v(5.9, 55.03) * mm});
            skLineSegment(sketch, "E27.24.0.1", {"start": v(5.9, 55.03) * mm, "end": v(-5.93, 55.03) * mm});
            skArc(sketch, "E27.24.0.2", {"start": v(-5.93, 55.03) * mm, "mid": v(-6.24, 54.9) * mm, "end": v(-6.37, 54.6) * mm});
            skLineSegment(sketch, "E27.24.0.3", {"start": v(-6.37, 54.6) * mm, "end": v(-6.37, 54.2) * mm});
            skArc(sketch, "E27.24.0.4", {"start": v(-6.37, 54.2) * mm, "mid": v(-6.24, 53.9) * mm, "end": v(-5.93, 53.76) * mm});
            skLineSegment(sketch, "E27.24.0.5", {"start": v(5.9, 53.76) * mm, "end": v(-5.93, 53.76) * mm});
            skArc(sketch, "E27.24.0.6", {"start": v(5.9, 53.76) * mm, "mid": v(6.2, 53.9) * mm, "end": v(6.33, 54.2) * mm});
            skLineSegment(sketch, "E27.24.0.7", {"start": v(6.33, 54.6) * mm, "end": v(6.33, 54.2) * mm});
            skArc(sketch, "E27.25.0.0", {"start": v(6.33, 52.3) * mm, "mid": v(6.2, 52.62) * mm, "end": v(5.89, 52.75) * mm});
            skLineSegment(sketch, "E27.25.0.1", {"start": v(5.89, 52.75) * mm, "end": v(-5.93, 52.75) * mm});
            skArc(sketch, "E27.25.0.2", {"start": v(-5.93, 52.75) * mm, "mid": v(-6.24, 52.62) * mm, "end": v(-6.37, 52.3) * mm});
            skLineSegment(sketch, "E27.25.0.3", {"start": v(-6.37, 52.3) * mm, "end": v(-6.37, 51.91) * mm});
            skArc(sketch, "E27.25.0.4", {"start": v(-6.37, 51.91) * mm, "mid": v(-6.24, 51.6) * mm, "end": v(-5.93, 51.48) * mm});
            skLineSegment(sketch, "E27.25.0.5", {"start": v(5.89, 51.48) * mm, "end": v(-5.93, 51.48) * mm});
            skArc(sketch, "E27.25.0.6", {"start": v(5.89, 51.48) * mm, "mid": v(6.2, 51.6) * mm, "end": v(6.33, 51.91) * mm});
            skLineSegment(sketch, "E27.25.0.7", {"start": v(6.33, 52.3) * mm, "end": v(6.33, 51.91) * mm});
            skArc(sketch, "E27.26.0.0", {"start": v(6.33, 50.02) * mm, "mid": v(6.2, 50.33) * mm, "end": v(5.89, 50.46) * mm});
            skLineSegment(sketch, "E27.26.0.1", {"start": v(5.89, 50.46) * mm, "end": v(-5.93, 50.46) * mm});
            skArc(sketch, "E27.26.0.2", {"start": v(-5.93, 50.46) * mm, "mid": v(-6.24, 50.33) * mm, "end": v(-6.37, 50.02) * mm});
            skLineSegment(sketch, "E27.26.0.3", {"start": v(-6.37, 50.02) * mm, "end": v(-6.37, 49.63) * mm});
            skArc(sketch, "E27.26.0.4", {"start": v(-6.37, 49.63) * mm, "mid": v(-6.24, 49.32) * mm, "end": v(-5.93, 49.19) * mm});
            skLineSegment(sketch, "E27.26.0.5", {"start": v(5.89, 49.19) * mm, "end": v(-5.93, 49.19) * mm});
            skArc(sketch, "E27.26.0.6", {"start": v(5.89, 49.19) * mm, "mid": v(6.2, 49.32) * mm, "end": v(6.33, 49.63) * mm});
            skLineSegment(sketch, "E27.26.0.7", {"start": v(6.33, 50.02) * mm, "end": v(6.33, 49.63) * mm});
            skArc(sketch, "E27.27.0.0", {"start": v(6.33, 47.73) * mm, "mid": v(6.2, 48.05) * mm, "end": v(5.89, 48.17) * mm});
            skLineSegment(sketch, "E27.27.0.1", {"start": v(5.89, 48.17) * mm, "end": v(-5.93, 48.17) * mm});
            skArc(sketch, "E27.27.0.2", {"start": v(-5.93, 48.17) * mm, "mid": v(-6.24, 48.05) * mm, "end": v(-6.37, 47.73) * mm});
            skLineSegment(sketch, "E27.27.0.3", {"start": v(-6.37, 47.73) * mm, "end": v(-6.37, 47.34) * mm});
            skArc(sketch, "E27.27.0.4", {"start": v(-6.37, 47.34) * mm, "mid": v(-6.24, 47.03) * mm, "end": v(-5.93, 46.9) * mm});
            skLineSegment(sketch, "E27.27.0.5", {"start": v(5.89, 46.9) * mm, "end": v(-5.93, 46.9) * mm});
            skArc(sketch, "E27.27.0.6", {"start": v(5.89, 46.9) * mm, "mid": v(6.2, 47.03) * mm, "end": v(6.33, 47.34) * mm});
            skLineSegment(sketch, "E27.27.0.7", {"start": v(6.33, 47.73) * mm, "end": v(6.33, 47.34) * mm});
            skArc(sketch, "E27.28.0.0", {"start": v(6.33, 45.45) * mm, "mid": v(6.2, 45.76) * mm, "end": v(5.89, 45.89) * mm});
            skLineSegment(sketch, "E27.28.0.1", {"start": v(5.89, 45.89) * mm, "end": v(-5.93, 45.89) * mm});
            skArc(sketch, "E27.28.0.2", {"start": v(-5.93, 45.89) * mm, "mid": v(-6.24, 45.76) * mm, "end": v(-6.37, 45.45) * mm});
            skLineSegment(sketch, "E27.28.0.3", {"start": v(-6.37, 45.45) * mm, "end": v(-6.37, 45.06) * mm});
            skArc(sketch, "E27.28.0.4", {"start": v(-6.37, 45.06) * mm, "mid": v(-6.24, 44.75) * mm, "end": v(-5.93, 44.62) * mm});
            skLineSegment(sketch, "E27.28.0.5", {"start": v(5.89, 44.62) * mm, "end": v(-5.93, 44.62) * mm});
            skArc(sketch, "E27.28.0.6", {"start": v(5.89, 44.62) * mm, "mid": v(6.2, 44.75) * mm, "end": v(6.33, 45.06) * mm});
            skLineSegment(sketch, "E27.28.0.7", {"start": v(6.33, 45.45) * mm, "end": v(6.33, 45.06) * mm});
            skArc(sketch, "E27.29.0.0", {"start": v(6.33, 43.16) * mm, "mid": v(6.2, 43.47) * mm, "end": v(5.89, 43.6) * mm});
            skLineSegment(sketch, "E27.29.0.1", {"start": v(5.89, 43.6) * mm, "end": v(-5.94, 43.6) * mm});
            skArc(sketch, "E27.29.0.2", {"start": v(-5.94, 43.6) * mm, "mid": v(-6.25, 43.47) * mm, "end": v(-6.37, 43.16) * mm});
            skLineSegment(sketch, "E27.29.0.3", {"start": v(-6.37, 43.16) * mm, "end": v(-6.37, 42.77) * mm});
            skArc(sketch, "E27.29.0.4", {"start": v(-6.37, 42.77) * mm, "mid": v(-6.25, 42.46) * mm, "end": v(-5.94, 42.33) * mm});
            skLineSegment(sketch, "E27.29.0.5", {"start": v(5.89, 42.33) * mm, "end": v(-5.94, 42.33) * mm});
            skArc(sketch, "E27.29.0.6", {"start": v(5.89, 42.33) * mm, "mid": v(6.2, 42.46) * mm, "end": v(6.33, 42.77) * mm});
            skLineSegment(sketch, "E27.29.0.7", {"start": v(6.33, 43.16) * mm, "end": v(6.33, 42.77) * mm});
            skArc(sketch, "E27.30.0.0", {"start": v(6.32, 40.88) * mm, "mid": v(6.2, 41.19) * mm, "end": v(5.89, 41.32) * mm});
            skLineSegment(sketch, "E27.30.0.1", {"start": v(5.89, 41.32) * mm, "end": v(-5.94, 41.32) * mm});
            skArc(sketch, "E27.30.0.2", {"start": v(-5.94, 41.32) * mm, "mid": v(-6.25, 41.19) * mm, "end": v(-6.38, 40.88) * mm});
            skLineSegment(sketch, "E27.30.0.3", {"start": v(-6.38, 40.88) * mm, "end": v(-6.38, 40.48) * mm});
            skArc(sketch, "E27.30.0.4", {"start": v(-6.38, 40.48) * mm, "mid": v(-6.25, 40.17) * mm, "end": v(-5.94, 40.05) * mm});
            skLineSegment(sketch, "E27.30.0.5", {"start": v(5.89, 40.05) * mm, "end": v(-5.94, 40.05) * mm});
            skArc(sketch, "E27.30.0.6", {"start": v(5.89, 40.05) * mm, "mid": v(6.2, 40.17) * mm, "end": v(6.32, 40.48) * mm});
            skLineSegment(sketch, "E27.30.0.7", {"start": v(6.32, 40.88) * mm, "end": v(6.32, 40.48) * mm});
            skArc(sketch, "E27.31.0.0", {"start": v(6.32, 38.6) * mm, "mid": v(6.2, 38.9) * mm, "end": v(5.88, 39.03) * mm});
            skLineSegment(sketch, "E27.31.0.1", {"start": v(5.88, 39.03) * mm, "end": v(-5.94, 39.03) * mm});
            skArc(sketch, "E27.31.0.2", {"start": v(-5.94, 39.03) * mm, "mid": v(-6.25, 38.9) * mm, "end": v(-6.38, 38.6) * mm});
            skLineSegment(sketch, "E27.31.0.3", {"start": v(-6.38, 38.6) * mm, "end": v(-6.38, 38.2) * mm});
            skArc(sketch, "E27.31.0.4", {"start": v(-6.38, 38.2) * mm, "mid": v(-6.25, 37.89) * mm, "end": v(-5.94, 37.76) * mm});
            skLineSegment(sketch, "E27.31.0.5", {"start": v(5.88, 37.76) * mm, "end": v(-5.94, 37.76) * mm});
            skArc(sketch, "E27.31.0.6", {"start": v(5.88, 37.76) * mm, "mid": v(6.2, 37.89) * mm, "end": v(6.32, 38.2) * mm});
            skLineSegment(sketch, "E27.31.0.7", {"start": v(6.32, 38.6) * mm, "end": v(6.32, 38.2) * mm});
            skArc(sketch, "E27.32.0.0", {"start": v(6.32, 36.3) * mm, "mid": v(6.2, 36.62) * mm, "end": v(5.88, 36.74) * mm});
            skLineSegment(sketch, "E27.32.0.1", {"start": v(5.88, 36.74) * mm, "end": v(-5.94, 36.74) * mm});
            skArc(sketch, "E27.32.0.2", {"start": v(-5.94, 36.74) * mm, "mid": v(-6.25, 36.62) * mm, "end": v(-6.38, 36.3) * mm});
            skLineSegment(sketch, "E27.32.0.3", {"start": v(-6.38, 36.3) * mm, "end": v(-6.38, 35.91) * mm});
            skArc(sketch, "E27.32.0.4", {"start": v(-6.38, 35.91) * mm, "mid": v(-6.25, 35.6) * mm, "end": v(-5.94, 35.47) * mm});
            skLineSegment(sketch, "E27.32.0.5", {"start": v(5.88, 35.47) * mm, "end": v(-5.94, 35.47) * mm});
            skArc(sketch, "E27.32.0.6", {"start": v(5.88, 35.47) * mm, "mid": v(6.2, 35.6) * mm, "end": v(6.32, 35.91) * mm});
            skLineSegment(sketch, "E27.32.0.7", {"start": v(6.32, 36.3) * mm, "end": v(6.32, 35.91) * mm});
            skArc(sketch, "E27.33.0.0", {"start": v(6.32, 34.02) * mm, "mid": v(6.2, 34.33) * mm, "end": v(5.88, 34.46) * mm});
            skLineSegment(sketch, "E27.33.0.1", {"start": v(5.88, 34.46) * mm, "end": v(-5.94, 34.46) * mm});
            skArc(sketch, "E27.33.0.2", {"start": v(-5.94, 34.46) * mm, "mid": v(-6.25, 34.33) * mm, "end": v(-6.38, 34.02) * mm});
            skLineSegment(sketch, "E27.33.0.3", {"start": v(-6.38, 34.02) * mm, "end": v(-6.38, 33.63) * mm});
            skArc(sketch, "E27.33.0.4", {"start": v(-6.38, 33.63) * mm, "mid": v(-6.25, 33.32) * mm, "end": v(-5.94, 33.19) * mm});
            skLineSegment(sketch, "E27.33.0.5", {"start": v(5.88, 33.19) * mm, "end": v(-5.94, 33.19) * mm});
            skArc(sketch, "E27.33.0.6", {"start": v(5.88, 33.19) * mm, "mid": v(6.2, 33.32) * mm, "end": v(6.32, 33.63) * mm});
            skLineSegment(sketch, "E27.33.0.7", {"start": v(6.32, 34.02) * mm, "end": v(6.32, 33.63) * mm});
            skArc(sketch, "E27.34.0.0", {"start": v(6.32, 31.73) * mm, "mid": v(6.2, 32.04) * mm, "end": v(5.88, 32.17) * mm});
            skLineSegment(sketch, "E27.34.0.1", {"start": v(5.88, 32.17) * mm, "end": v(-5.94, 32.17) * mm});
            skArc(sketch, "E27.34.0.2", {"start": v(-5.94, 32.17) * mm, "mid": v(-6.25, 32.04) * mm, "end": v(-6.38, 31.73) * mm});
            skLineSegment(sketch, "E27.34.0.3", {"start": v(-6.38, 31.73) * mm, "end": v(-6.38, 31.34) * mm});
            skArc(sketch, "E27.34.0.4", {"start": v(-6.38, 31.34) * mm, "mid": v(-6.25, 31.03) * mm, "end": v(-5.94, 30.9) * mm});
            skLineSegment(sketch, "E27.34.0.5", {"start": v(5.88, 30.9) * mm, "end": v(-5.94, 30.9) * mm});
            skArc(sketch, "E27.34.0.6", {"start": v(5.88, 30.9) * mm, "mid": v(6.2, 31.03) * mm, "end": v(6.32, 31.34) * mm});
            skLineSegment(sketch, "E27.34.0.7", {"start": v(6.32, 31.73) * mm, "end": v(6.32, 31.34) * mm});
            skArc(sketch, "E27.35.0.0", {"start": v(6.32, 29.45) * mm, "mid": v(6.2, 29.76) * mm, "end": v(5.88, 29.89) * mm});
            skLineSegment(sketch, "E27.35.0.1", {"start": v(5.88, 29.89) * mm, "end": v(-5.94, 29.89) * mm});
            skArc(sketch, "E27.35.0.2", {"start": v(-5.94, 29.89) * mm, "mid": v(-6.25, 29.76) * mm, "end": v(-6.38, 29.45) * mm});
            skLineSegment(sketch, "E27.35.0.3", {"start": v(-6.38, 29.45) * mm, "end": v(-6.38, 29.05) * mm});
            skArc(sketch, "E27.35.0.4", {"start": v(-6.38, 29.05) * mm, "mid": v(-6.25, 28.74) * mm, "end": v(-5.94, 28.62) * mm});
            skLineSegment(sketch, "E27.35.0.5", {"start": v(5.88, 28.62) * mm, "end": v(-5.94, 28.62) * mm});
            skArc(sketch, "E27.35.0.6", {"start": v(5.88, 28.62) * mm, "mid": v(6.2, 28.74) * mm, "end": v(6.32, 29.05) * mm});
            skLineSegment(sketch, "E27.35.0.7", {"start": v(6.32, 29.45) * mm, "end": v(6.32, 29.05) * mm});
            skArc(sketch, "E27.36.0.0", {"start": v(6.32, 27.16) * mm, "mid": v(6.2, 27.47) * mm, "end": v(5.88, 27.6) * mm});
            skLineSegment(sketch, "E27.36.0.1", {"start": v(5.88, 27.6) * mm, "end": v(-5.94, 27.6) * mm});
            skArc(sketch, "E27.36.0.2", {"start": v(-5.94, 27.6) * mm, "mid": v(-6.25, 27.47) * mm, "end": v(-6.38, 27.16) * mm});
            skLineSegment(sketch, "E27.36.0.3", {"start": v(-6.38, 27.16) * mm, "end": v(-6.38, 26.77) * mm});
            skArc(sketch, "E27.36.0.4", {"start": v(-6.38, 26.77) * mm, "mid": v(-6.25, 26.46) * mm, "end": v(-5.94, 26.33) * mm});
            skLineSegment(sketch, "E27.36.0.5", {"start": v(5.88, 26.33) * mm, "end": v(-5.94, 26.33) * mm});
            skArc(sketch, "E27.36.0.6", {"start": v(5.88, 26.33) * mm, "mid": v(6.2, 26.46) * mm, "end": v(6.32, 26.77) * mm});
            skLineSegment(sketch, "E27.36.0.7", {"start": v(6.32, 27.16) * mm, "end": v(6.32, 26.77) * mm});
            skArc(sketch, "E27.37.0.0", {"start": v(6.32, 24.87) * mm, "mid": v(6.2, 25.19) * mm, "end": v(5.88, 25.31) * mm});
            skLineSegment(sketch, "E27.37.0.1", {"start": v(5.88, 25.31) * mm, "end": v(-5.94, 25.31) * mm});
            skArc(sketch, "E27.37.0.2", {"start": v(-5.94, 25.31) * mm, "mid": v(-6.25, 25.19) * mm, "end": v(-6.38, 24.87) * mm});
            skLineSegment(sketch, "E27.37.0.3", {"start": v(-6.38, 24.87) * mm, "end": v(-6.38, 24.48) * mm});
            skArc(sketch, "E27.37.0.4", {"start": v(-6.38, 24.48) * mm, "mid": v(-6.25, 24.17) * mm, "end": v(-5.94, 24.04) * mm});
            skLineSegment(sketch, "E27.37.0.5", {"start": v(5.88, 24.04) * mm, "end": v(-5.94, 24.04) * mm});
            skArc(sketch, "E27.37.0.6", {"start": v(5.88, 24.04) * mm, "mid": v(6.2, 24.17) * mm, "end": v(6.32, 24.48) * mm});
            skLineSegment(sketch, "E27.37.0.7", {"start": v(6.32, 24.87) * mm, "end": v(6.32, 24.48) * mm});
            skArc(sketch, "E27.38.0.0", {"start": v(6.32, 22.59) * mm, "mid": v(6.19, 22.9) * mm, "end": v(5.88, 23.03) * mm});
            skLineSegment(sketch, "E27.38.0.1", {"start": v(5.88, 23.03) * mm, "end": v(-5.94, 23.03) * mm});
            skArc(sketch, "E27.38.0.2", {"start": v(-5.94, 23.03) * mm, "mid": v(-6.25, 22.9) * mm, "end": v(-6.38, 22.59) * mm});
            skLineSegment(sketch, "E27.38.0.3", {"start": v(-6.38, 22.59) * mm, "end": v(-6.38, 22.2) * mm});
            skArc(sketch, "E27.38.0.4", {"start": v(-6.38, 22.2) * mm, "mid": v(-6.25, 21.89) * mm, "end": v(-5.94, 21.76) * mm});
            skLineSegment(sketch, "E27.38.0.5", {"start": v(5.88, 21.76) * mm, "end": v(-5.94, 21.76) * mm});
            skArc(sketch, "E27.38.0.6", {"start": v(5.88, 21.76) * mm, "mid": v(6.19, 21.89) * mm, "end": v(6.32, 22.2) * mm});
            skLineSegment(sketch, "E27.38.0.7", {"start": v(6.32, 22.59) * mm, "end": v(6.32, 22.2) * mm});
            skArc(sketch, "E27.39.0.0", {"start": v(6.32, 20.3) * mm, "mid": v(6.19, 20.61) * mm, "end": v(5.88, 20.74) * mm});
            skLineSegment(sketch, "E27.39.0.1", {"start": v(5.88, 20.74) * mm, "end": v(-5.94, 20.74) * mm});
            skArc(sketch, "E27.39.0.2", {"start": v(-5.94, 20.74) * mm, "mid": v(-6.25, 20.61) * mm, "end": v(-6.38, 20.3) * mm});
            skLineSegment(sketch, "E27.39.0.3", {"start": v(-6.38, 20.3) * mm, "end": v(-6.38, 19.91) * mm});
            skArc(sketch, "E27.39.0.4", {"start": v(-6.38, 19.91) * mm, "mid": v(-6.25, 19.6) * mm, "end": v(-5.94, 19.47) * mm});
            skLineSegment(sketch, "E27.39.0.5", {"start": v(5.88, 19.47) * mm, "end": v(-5.94, 19.47) * mm});
            skArc(sketch, "E27.39.0.6", {"start": v(5.88, 19.47) * mm, "mid": v(6.19, 19.6) * mm, "end": v(6.32, 19.91) * mm});
            skLineSegment(sketch, "E27.39.0.7", {"start": v(6.32, 20.3) * mm, "end": v(6.32, 19.91) * mm});
            skLineSegment(sketch, "E27.direction1", {"start": v(-5.91, 108.63) * mm, "end": v(-5.91, 106.34) * mm, "construction": true});
            skSolve(sketch);
        }
        {
            var Q0;
            Q0=qSketchRegion(id+"F13",true);
            extrude(context, id + "F14", {"entities" : qUnion([Q0]), "operationType" : NewBodyOperationType.REMOVE, "depth" : 12.7 * mm, "offsetDistance" : 25.4 * mm, "hasSecondDirection" : true, "secondDirectionOppositeDirection" : true, "secondDirectionDepth" : 12.7 * mm});
        }
    });
